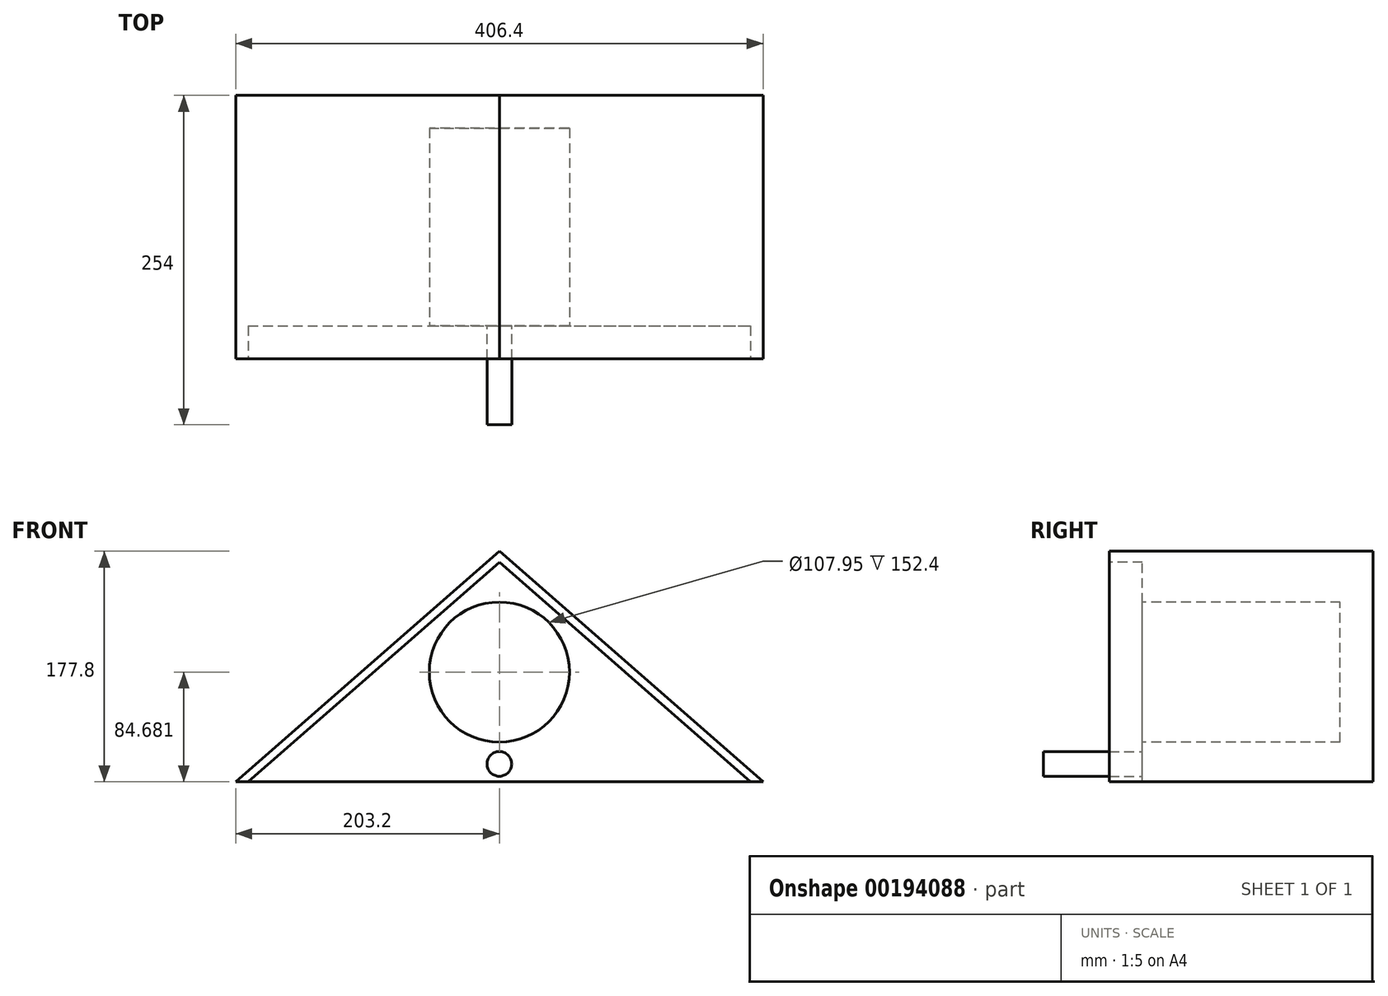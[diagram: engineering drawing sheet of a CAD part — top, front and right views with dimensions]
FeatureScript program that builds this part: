
annotation { "Feature Type Name" : "Feature", "Feature Type Description" : "" }
export const myFeature = defineFeature(function(context is Context, id is Id, definition is map)
    precondition{}
    {
        {
            var Q0;
            Q0=qCreatedBy(makeId("Front.planeOp"),FACE);
            var sketch = newSketch(context, id + "F0", { "sketchPlane" : qUnion([Q0])});
            skLineSegment(sketch, "E0", {"start": v(-203.2, 0) * mm, "end": v(203.2, 0) * mm});
            skLineSegment(sketch, "E1", {"start": v(203.2, 0) * mm, "end": v(0, 177.8) * mm});
            skLineSegment(sketch, "E2", {"start": v(0, 177.8) * mm, "end": v(-203.2, 0) * mm});
            skSolve(sketch);
        }
        {
            var Q0;
            Q0=makeQuery(id+"F0.imprint","IMPRINT",FACE,{"disambiguationData":[TD([[makeQuery(id+"F0.imprint","IMPRINT",EDGE,{"derivedFrom":sQuery(id+"F0.wireOp",EDGE,"E0")}),1.0]])]});
            extrude(context, id + "F1", {"entities" : qUnion([Q0]), "depth" : 203.2 * mm});
        }
        {
            var Q0;
            Q0=makeQuery(id+"F1.opExtrude","CAP_FACE",FACE,{"disambiguationData":[OSD([sQuery(id+"F0.wireOp",EDGE,"E0"),sQuery(id+"F0.wireOp",EDGE,"E1"),sQuery(id+"F0.wireOp",EDGE,"E2")])],"isStart":false});
            var sketch = newSketch(context, id + "F2", { "sketchPlane" : qUnion([Q0])});
            skLineSegment(sketch, "E3", {"start": v(-193.56, 0) * mm, "end": v(0, 169.36) * mm});
            skLineSegment(sketch, "E4", {"start": v(0, 169.36) * mm, "end": v(193.56, 0) * mm});
            skLineSegment(sketch, "E5", {"start": v(193.56, 0) * mm, "end": v(-193.56, 0) * mm});
            skPoint(sketch, "E6", {"position": v(0, 0) * mm});
            skSolve(sketch);
        }
        {
            var Q0;
            Q0 = qSketchRegion(id + "F2", true);
            extrude(context, id + "F3", {"entities" : qUnion([Q0]), "operationType" : NewBodyOperationType.REMOVE, "oppositeDirection" : true, "depth" : 25.4 * mm});
        }
        {
            var Q0;
            Q0=makeQuery(id+"F3.boolean.opBoolean","COPY",FACE,{"derivedFrom":makeQuery(id+"F3.opExtrude","CAP_FACE",FACE,{"disambiguationData":[OSD([sQuery(id+"F2.wireOp",EDGE,"E3"),sQuery(id+"F2.wireOp",EDGE,"E4"),sQuery(id+"F2.wireOp",EDGE,"E5")])],"isStart":false})});
            var sketch = newSketch(context, id + "F4", { "sketchPlane" : qUnion([Q0])});
            skLineSegment(sketch, "E7", {"start": v(0, 169.36) * mm, "end": v(0, 0) * mm, "construction": true});
            skPoint(sketch, "E8", {"position": v(0, 84.68) * mm});
            skCircle(sketch, "E9", {"center": v(0, 84.68) * mm, "radius": 53.98 * mm});
            skCircle(sketch, "E10", {"center": v(0, 13.83) * mm, "radius": 9.53 * mm});
            skSolve(sketch);
        }
        {
            var Q0;
            Q0=makeQuery(id+"F4.imprint","IMPRINT",FACE,{"disambiguationData":[TD([[makeQuery(id+"F4.imprint","IMPRINT",EDGE,{"derivedFrom":sQuery(id+"F4.wireOp",EDGE,"E9")}),1.0]])]});
            extrude(context, id + "F5", {"entities" : qUnion([Q0]), "operationType" : NewBodyOperationType.REMOVE, "oppositeDirection" : true, "depth" : 152.4 * mm});
        }
        {
            var Q0;
            Q0=makeQuery(id+"F4.imprint","IMPRINT",FACE,{"disambiguationData":[TD([[makeQuery(id+"F4.imprint","IMPRINT",EDGE,{"derivedFrom":sQuery(id+"F4.wireOp",EDGE,"E10")}),1.0]])]});
            extrude(context, id + "F6", {"entities" : qUnion([Q0]), "operationType" : NewBodyOperationType.ADD, "depth" : 76.2 * mm});
        }
    });
